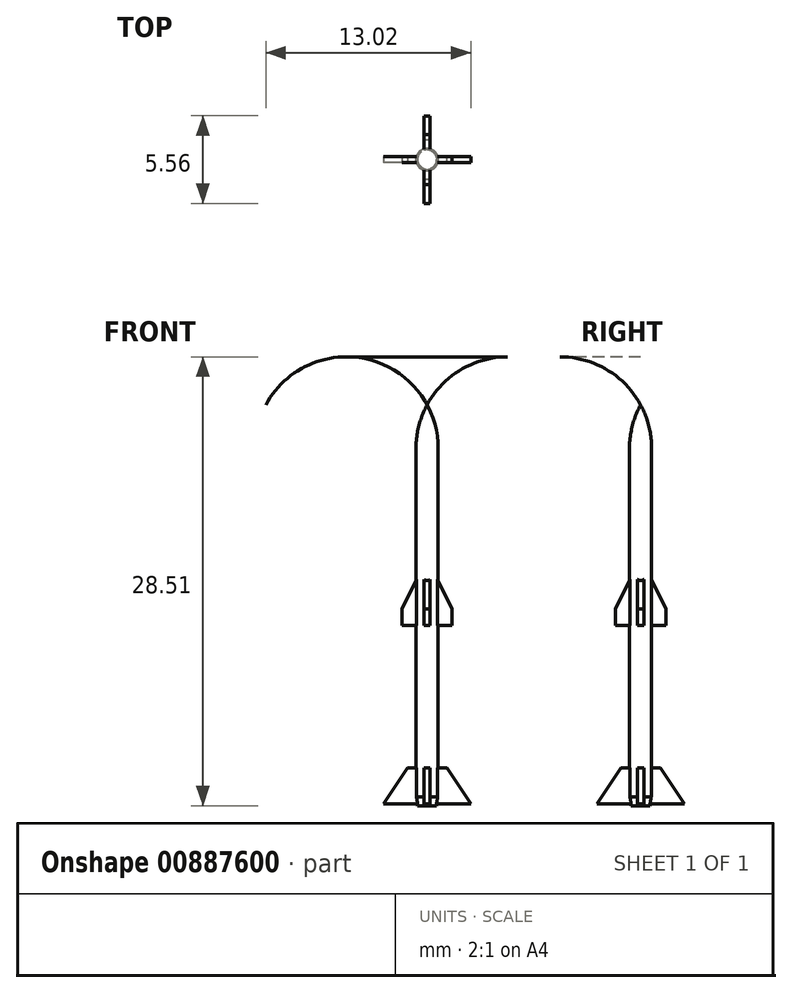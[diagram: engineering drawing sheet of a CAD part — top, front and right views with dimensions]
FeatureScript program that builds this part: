
annotation { "Feature Type Name" : "Feature", "Feature Type Description" : "" }
export const myFeature = defineFeature(function(context is Context, id is Id, definition is map)
    precondition{}
    {
        {
            var Q0;
            Q0=qCreatedBy(makeId("Front.planeOp"),FACE);
            var sketch = newSketch(context, id + "F0", { "sketchPlane" : qUnion([Q0])});
            skLineSegment(sketch, "E0", {"start": v(0, 0) * mm, "end": v(0, 25.47) * mm});
            skLineSegment(sketch, "E1", {"start": v(0.7, 22.69) * mm, "end": v(0.7, 0) * mm});
            skLineSegment(sketch, "E2", {"start": v(0.7, 0) * mm, "end": v(0, 0) * mm});
            skArc(sketch, "E3", {"start": v(0.7, 22.69) * mm, "mid": v(0.53, 24.12) * mm, "end": v(0, 25.47) * mm});
            skLineSegment(sketch, "E4", {"start": v(0.6, 0) * mm, "end": v(0.7, 0.56) * mm});
            skSolve(sketch);
        }
        {
            var Q0;
            {var subQ0=sQuery(id+"F0.wireOp",EDGE,"mrwio9nY-PsAZ-Zbfy-NhIU-sYq0QVbgGXAG");Q0=makeQuery(id+"F0.imprint","IMPRINT",FACE,{"disambiguationData":[TD([[makeQuery(id+"F0.imprint","IMPRINT",EDGE,{"derivedFrom":subQ0}),-1.0]])]});}
            var Q1;
            Q1=makeQuery(id+"F0.imprint","IMPRINT",FACE,{"disambiguationData":[TD([[makeQuery(id+"F0.imprint","IMPRINT",EDGE,{"derivedFrom":sQuery(id+"F0.wireOp",EDGE,"rEedh4zr-IGRr-Hqzj-sDLB-QnI7VE1V64O6.bottom")}),-1.0]])]});
            var Q2;
            Q2=makeQuery(id+"F0.imprint","IMPRINT",FACE,{"disambiguationData":[TD([[makeQuery(id+"F0.imprint","IMPRINT",EDGE,{"derivedFrom":sQuery(id+"F0.wireOp",EDGE,"E0")}),-1.0]])]});
            var Q3;
            Q3=makeQuery(id+"F0.imprint","IMPRINT",FACE,{"disambiguationData":[TD([[makeQuery(id+"F0.imprint","IMPRINT",EDGE,{"derivedFrom":sQuery(id+"F0.wireOp",EDGE,"p5wuz8j9-3HT4-kWwn-DjtP-lJmqTNSXSBJY.bottom")}),-1.0]])]});
            var Q4;
            Q4=sQuery(id+"F0.wireOp",EDGE,"E0");
            revolve(context, id + "F1", {"surfaceOperationType" : NewSurfaceOperationType.NEW, "entities" : qUnion([Q0, Q1, Q2, Q3]), "axis" : qUnion([Q4]), "revolveType" : RevolveType.FULL});
        }
        {
            var Q0;
            Q0=qCreatedBy(makeId("Front.planeOp"),FACE);
            var sketch = newSketch(context, id + "F2", { "sketchPlane" : qUnion([Q0])});
            skLineSegment(sketch, "E5", {"start": v(0, 0) * mm, "end": v(0, 22.29) * mm});
            skLineSegment(sketch, "E6", {"start": v(0.7, -0.2) * mm, "end": v(0.7, 32.87) * mm, "construction": true});
            skLineSegment(sketch, "E7", {"start": v(0.7, -0.2) * mm, "end": v(0.7, 0) * mm});
            skLineSegment(sketch, "E8", {"start": v(0, 11.46) * mm, "end": v(1.6, 11.46) * mm});
            skLineSegment(sketch, "E9", {"start": v(0, 0.1) * mm, "end": v(2.78, 0.1) * mm});
            skLineSegment(sketch, "E10", {"start": v(0, 2.4) * mm, "end": v(1.25, 2.4) * mm});
            skLineSegment(sketch, "E11", {"start": v(1.25, 2.4) * mm, "end": v(2.78, 0.1) * mm});
            skLineSegment(sketch, "E12", {"start": v(1.6, 11.46) * mm, "end": v(1.6, 12.5) * mm});
            skLineSegment(sketch, "E13", {"start": v(1.6, 12.5) * mm, "end": v(0, 15.73) * mm});
            skPoint(sketch, "E14", {"position": v(0.7, 14.3) * mm});
            skLineSegment(sketch, "E15.0", {"start": v(0.7, 0.56) * mm, "end": v(-0.7, 0.56) * mm});
            skSolve(sketch);
        }
        {
            var Q0;
            Q0=qSketchRegion(id+"F2",true);
            extrude(context, id + "F3", {"entities" : qUnion([Q0]), "operationType" : NewBodyOperationType.ADD, "depth" : .4 * mm, "offsetDistance" : 25 * mm, "symmetric" : true});
        }
        {
            var Q0;
            Q0=makeQuery(id+"F1.opRevolve","SWEPT_BODY",BODY,{"disambiguationData":[OSD([sQuery(id+"F0.wireOp",EDGE,"E0"),sQuery(id+"F0.wireOp",EDGE,"E1"),sQuery(id+"F0.wireOp",EDGE,"E2"),sQuery(id+"F0.wireOp",EDGE,"2EiOItwe-9FNA-eY8p-DkXH-AMy5AHyUmzZA"),sQuery(id+"F0.wireOp",EDGE,"lF35QjYl-MEgV-fRWE-0Yr6-Bt5vS8A7brRf")])]});
            var Q1;
            Q1=makeQuery(id+"F1.opRevolve","SWEPT_FACE",FACE,{"disambiguationData":[OSD([sQuery(id+"F0.wireOp",EDGE,"E1")])]});
            circularPattern(context, id + "F4", {"operationType" : NewBodyOperationType.ADD, "entities" : qUnion([Q0]), "axis" : qUnion([Q1]), "angle" : 360 * degree, "instanceCount" : 4, "equalSpace" : true, "computeTransformsWithoutBuiltin" : true});
        }
    });
